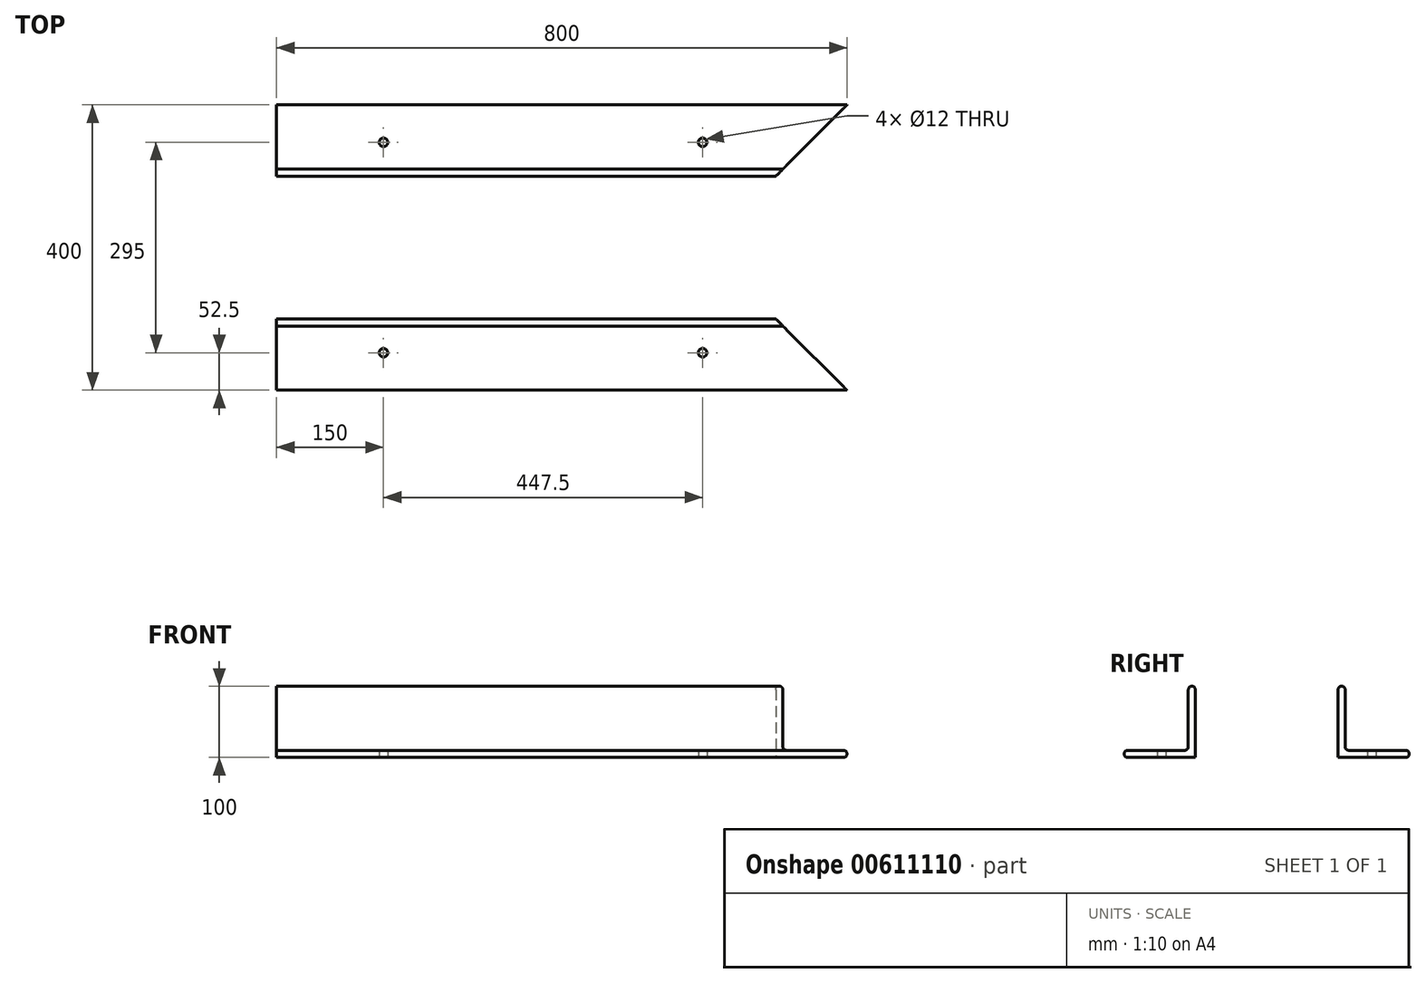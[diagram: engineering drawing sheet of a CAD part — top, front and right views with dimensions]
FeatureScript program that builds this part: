
annotation { "Feature Type Name" : "Feature", "Feature Type Description" : "" }
export const myFeature = defineFeature(function(context is Context, id is Id, definition is map)
    precondition{}
    {
        {
            var Q0;
            Q0=qCreatedBy(makeId("Right.planeOp"),FACE);
            var sketch = newSketch(context, id + "F0", { "sketchPlane" : qUnion([Q0])});
            skLineSegment(sketch, "E0", {"start": v(0, 95) * mm, "end": v(0, 0) * mm});
            skLineSegment(sketch, "E1", {"start": v(0, 0) * mm, "end": v(95, 0) * mm});
            skLineSegment(sketch, "E2", {"start": v(100, 5) * mm, "end": v(100, 5) * mm});
            skLineSegment(sketch, "E3", {"start": v(95, 10) * mm, "end": v(15, 10) * mm});
            skLineSegment(sketch, "E4", {"start": v(10, 15) * mm, "end": v(10, 95) * mm});
            skLineSegment(sketch, "E5", {"start": v(5, 100) * mm, "end": v(5, 100) * mm});
            skPoint(sketch, "E6.visualSharp", {"position": v(0, 100) * mm});
            skArc(sketch, "E6.filletArc", {"start": v(5, 100) * mm, "mid": v(1.46, 98.54) * mm, "end": v(0, 95) * mm});
            skPoint(sketch, "E7.visualSharp", {"position": v(10, 100) * mm});
            skArc(sketch, "E7.filletArc", {"start": v(10, 95) * mm, "mid": v(8.54, 98.54) * mm, "end": v(5, 100) * mm});
            skPoint(sketch, "E8.visualSharp", {"position": v(10, 10) * mm});
            skArc(sketch, "E8.filletArc", {"start": v(10, 15) * mm, "mid": v(11.46, 11.46) * mm, "end": v(15, 10) * mm});
            skPoint(sketch, "E9.visualSharp", {"position": v(100, 10) * mm});
            skArc(sketch, "E9.filletArc", {"start": v(100, 5) * mm, "mid": v(98.54, 8.54) * mm, "end": v(95, 10) * mm});
            skPoint(sketch, "E10.visualSharp", {"position": v(100, 0) * mm});
            skArc(sketch, "E10.filletArc", {"start": v(95, 0) * mm, "mid": v(98.54, 1.46) * mm, "end": v(100, 5) * mm});
            skSolve(sketch);
        }
        {
            var Q0;
            Q0=makeQuery(id+"F0.imprint","IMPRINT",FACE,{"disambiguationData":[TD([[makeQuery(id+"F0.imprint","IMPRINT",EDGE,{"derivedFrom":sQuery(id+"F0.wireOp",EDGE,"E0")}),1.0]])]});
            extrude(context, id + "F1", {"entities" : qUnion([Q0]), "endBound" : BoundingType.SYMMETRIC, "depth" : 800 * mm, "offsetDistance" : 25 * mm});
        }
        {
            var Q0;
            Q0=makeQuery(id+"F1.opExtrude","SWEPT_FACE",FACE,{"disambiguationData":[OSD([sQuery(id+"F0.wireOp",EDGE,"E1")])]});
            var sketch = newSketch(context, id + "F2", { "sketchPlane" : qUnion([Q0])});
            skLineSegment(sketch, "E11", {"start": v(400, -100) * mm, "end": v(400, 0) * mm});
            skLineSegment(sketch, "E12", {"start": v(400, 0) * mm, "end": v(300, 0) * mm});
            skLineSegment(sketch, "E13", {"start": v(300, 0) * mm, "end": v(400, -100) * mm});
            skSolve(sketch);
        }
        {
            var Q0;
            {var subQ0=sQuery(id+"F2.wireOp",EDGE,"E12");Q0=makeQuery(id+"F2.imprint","IMPRINT",FACE,{"disambiguationData":[TD([[makeQuery(id+"F2.imprint","IMPRINT",EDGE,{"derivedFrom":subQ0}),1.0]])]});}
            var Q1;
            {var subQ0=sQuery(id+"F2.wireOp",EDGE,"E11");var subQ3=sQuery(id+"F2.wireOp",EDGE,"E13");var subQ4=makeQuery(id+"F2.imprint","INTERSECT",VERTEX,{"derivedFrom":[subQ0,subQ3]});Q1=makeQuery(id+"F2.imprint","IMPRINT",FACE,{"disambiguationData":[TD([[makeQuery(id+"F2.imprint","IMPRINT",EDGE,{"disambiguationData":[TD([[subQ4,-1.0]])],"derivedFrom":subQ0}),1.0]])]});}
            extrude(context, id + "F3", {"entities" : qUnion([Q0, Q1]), "operationType" : NewBodyOperationType.REMOVE, "endBound" : BoundingType.THROUGH_ALL, "oppositeDirection" : true, "depth" : 25 * mm, "offsetDistance" : 25 * mm});
        }
        {
            var Q0;
            Q0=qCreatedBy(makeId("Front.planeOp"),FACE);
            cPlane(context, id + "F4", {"entities" : qUnion([Q0]), "cplaneType" : CPlaneType.OFFSET, "offset" : 100 * mm, "width" : 150 * mm, "height" : 150 * mm});
        }
        {
            var Q0;
            Q0=makeQuery(id+"F1.opExtrude","SWEPT_BODY",BODY,{"disambiguationData":[OSD([sQuery(id+"F0.wireOp",EDGE,"E0"),sQuery(id+"F0.wireOp",EDGE,"E1"),sQuery(id+"F0.wireOp",EDGE,"E3"),sQuery(id+"F0.wireOp",EDGE,"E4"),sQuery(id+"F0.wireOp",EDGE,"E6.filletArc"),sQuery(id+"F0.wireOp",EDGE,"E7.filletArc"),sQuery(id+"F0.wireOp",EDGE,"E8.filletArc"),sQuery(id+"F0.wireOp",EDGE,"E9.filletArc"),sQuery(id+"F0.wireOp",EDGE,"E10.filletArc")])]});
            var Q1;
            Q1=qCreatedBy(id+"F4.planeOp",FACE);
            mirror(context, id + "F5", {"entities" : qUnion([Q0]), "mirrorPlane" : qUnion([Q1])});
        }
        {
            var Q0;
            Q0=makeQuery(id+"F1.opExtrude","SWEPT_FACE",FACE,{"disambiguationData":[OSD([sQuery(id+"F0.wireOp",EDGE,"E1")])]});
            var sketch = newSketch(context, id + "F6", { "sketchPlane" : qUnion([Q0])});
            skPoint(sketch, "E14.endSnap0", {"position": v(347.5, -47.5) * mm});
            skCircle(sketch, "E15", {"center": v(-250, -47.5) * mm, "radius": 6 * mm});
            skCircle(sketch, "E16", {"center": v(197.5, -47.5) * mm, "radius": 6 * mm});
            skPoint(sketch, "E17.orphan", {"position": v(-400, -47.5) * mm});
            skSolve(sketch);
        }
        {
            var Q0;
            Q0=makeQuery(id+"F6.imprint","IMPRINT",FACE,{"disambiguationData":[TD([[makeQuery(id+"F6.imprint","IMPRINT",EDGE,{"derivedFrom":sQuery(id+"F6.wireOp",EDGE,"E15")}),1.0]])]});
            var Q1;
            Q1=makeQuery(id+"F6.imprint","IMPRINT",FACE,{"disambiguationData":[TD([[makeQuery(id+"F6.imprint","IMPRINT",EDGE,{"derivedFrom":sQuery(id+"F6.wireOp",EDGE,"E16")}),1.0]])]});
            extrude(context, id + "F7", {"entities" : qUnion([Q0, Q1]), "operationType" : NewBodyOperationType.REMOVE, "endBound" : BoundingType.THROUGH_ALL, "oppositeDirection" : true, "depth" : 25 * mm, "offsetDistance" : 25 * mm});
        }
        {
            var Q0;
            Q0=makeQuery(id+"F5.opPattern","COPY",FACE,{"derivedFrom":makeQuery(id+"F1.opExtrude","SWEPT_FACE",FACE,{"disambiguationData":[OSD([sQuery(id+"F0.wireOp",EDGE,"E1")])]}),"instanceName":"1"});
            var sketch = newSketch(context, id + "F8", { "sketchPlane" : qUnion([Q0])});
            skLineSegment(sketch, "E18", {"start": v(-400, 247.5) * mm, "end": v(-250, 247.5) * mm});
            skLineSegment(sketch, "E19", {"start": v(-250, 247.5) * mm, "end": v(197.5, 247.5) * mm});
            skLineSegment(sketch, "E20", {"start": v(197.5, 247.5) * mm, "end": v(347.5, 247.5) * mm});
            skCircle(sketch, "E21", {"center": v(-250, 247.5) * mm, "radius": 6 * mm});
            skCircle(sketch, "E22", {"center": v(197.5, 247.5) * mm, "radius": 6 * mm});
            skSolve(sketch);
        }
        {
            var Q0;
            Q0 = qSketchRegion(id + "F8", true);
            extrude(context, id + "F9", {"entities" : qUnion([Q0]), "operationType" : NewBodyOperationType.REMOVE, "endBound" : BoundingType.THROUGH_ALL, "oppositeDirection" : true, "depth" : 25 * mm, "offsetDistance" : 25 * mm});
        }
    });
